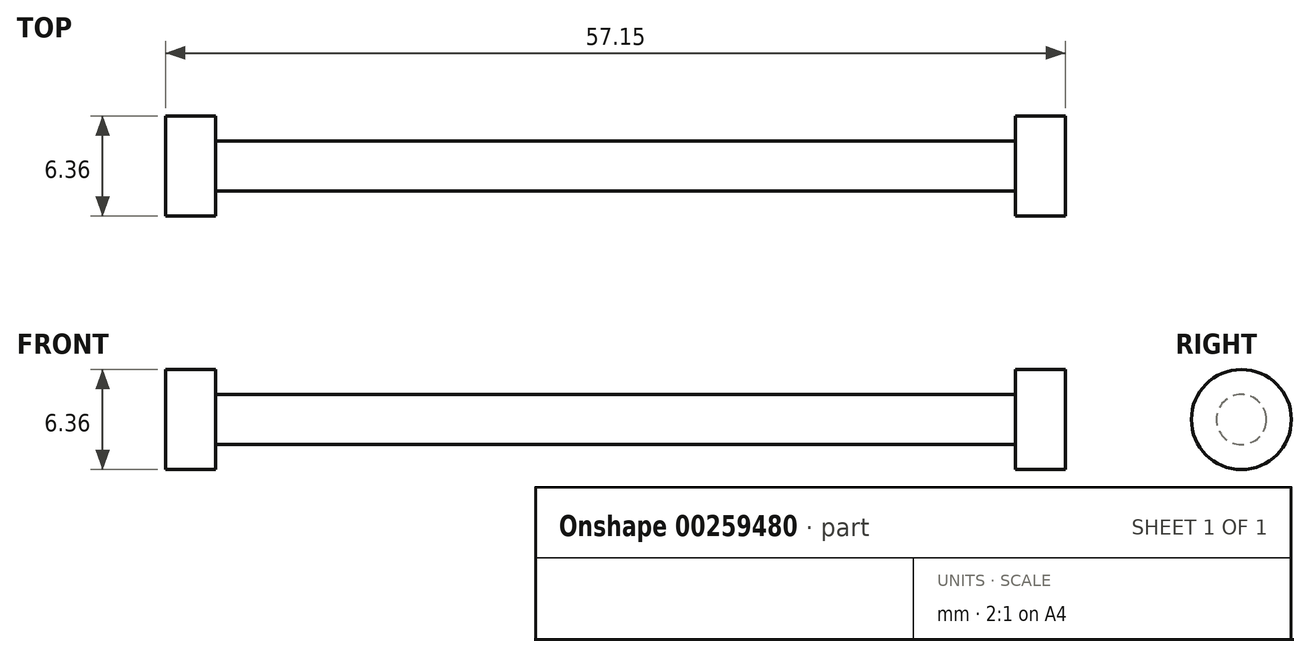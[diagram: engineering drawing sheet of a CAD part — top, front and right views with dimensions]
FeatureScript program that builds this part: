
annotation { "Feature Type Name" : "Feature", "Feature Type Description" : "" }
export const myFeature = defineFeature(function(context is Context, id is Id, definition is map)
    precondition{}
    {
        {
            var Q0;
            Q0=qCreatedBy(makeId("Right.planeOp"),FACE);
            var sketch = newSketch(context, id + "F0", { "sketchPlane" : qUnion([Q0])});
            skCircle(sketch, "E0", {"center": v(0, 0) * mm, "radius": 3.18 * mm});
            skSolve(sketch);
        }
        {
            var Q0;
            Q0=makeQuery(id+"F0.imprint","IMPRINT",FACE,{"disambiguationData":[TD([[makeQuery(id+"F0.imprint","IMPRINT",EDGE,{"derivedFrom":sQuery(id+"F0.wireOp",EDGE,"E0")}),1.0]])]});
            extrude(context, id + "F1", {"entities" : qUnion([Q0]), "depth" : 3.17 * mm});
        }
        {
            var Q0;
            Q0=makeQuery(id+"F1.opExtrude","CAP_FACE",FACE,{"disambiguationData":[OSD([sQuery(id+"F0.wireOp",EDGE,"E0")])],"isStart":false});
            var sketch = newSketch(context, id + "F2", { "sketchPlane" : qUnion([Q0])});
            skCircle(sketch, "E1", {"center": v(0, 0) * mm, "radius": 1.59 * mm});
            skSolve(sketch);
        }
        {
            var Q0;
            Q0=makeQuery(id+"F2.imprint","IMPRINT",FACE,{"disambiguationData":[TD([[makeQuery(id+"F2.imprint","IMPRINT",EDGE,{"derivedFrom":sQuery(id+"F2.wireOp",EDGE,"E1")}),1.0]])]});
            extrude(context, id + "F3", {"entities" : qUnion([Q0]), "operationType" : NewBodyOperationType.ADD, "depth" : 50.8 * mm});
        }
        {
            var Q0;
            Q0=makeQuery(id+"F3.opExtrude","CAP_FACE",FACE,{"disambiguationData":[OSD([sQuery(id+"F2.wireOp",EDGE,"E1")])],"isStart":false});
            var sketch = newSketch(context, id + "F4", { "sketchPlane" : qUnion([Q0])});
            skCircle(sketch, "E2", {"center": v(0, 0) * mm, "radius": 3.18 * mm});
            skSolve(sketch);
        }
        {
            var Q0;
            Q0=makeQuery(id+"F4.imprint","IMPRINT",FACE,{"disambiguationData":[TD([[makeQuery(id+"F4.imprint","IMPRINT",EDGE,{"derivedFrom":sQuery(id+"F4.wireOp",EDGE,"E2")}),1.0]])]});
            var Q1;
            Q1=makeQuery(id+"F4.imprint","IMPRINT",FACE,{"disambiguationData":[TD([[makeQuery(id+"F4.imprint","IMPRINT",EDGE,{"derivedFrom":makeQuery(id+"F3.opExtrude","CAP_EDGE",EDGE,{"disambiguationData":[OSD([sQuery(id+"F2.wireOp",EDGE,"E1")])],"isStart":false})}),1.0]])]});
            extrude(context, id + "F5", {"entities" : qUnion([Q0, Q1]), "operationType" : NewBodyOperationType.ADD, "depth" : 3.17 * mm});
        }
    });
